# Revit family: Gira_053500
name_source: partatom
category: Electrical Fixtures
revit_build: Autodesk Revit 2017 (Build: 20160225_1515(x64)
units: mm (PartAtom-declared; Revit-internal decimal feet)

## family parameters
Cut with Voids When Loaded = No
Host = Face
Maintain Annotation Orientation = No
Part Type = Normal
Room Calculation Point = No
Round Connector Dimension = Use Diameter
Shared = No

## types (1)
- DC pow.supply 24 V 5 A DRA Electronics
    BIM = https://media.live.bim.site 00_REG 6.rfa
    BIMSITE_PRODUCT_ID = 66304a2bba27a85c9a5d9a86d3c19f51ab19208a
    Cost = 0 $
    Default Elevation = 1219 mm
    Description = DC PSU 24V 5A DRA Elec. Power supply DC 24 V 5 A,DRA Features: - Stabilised and short-circuit-proof switched mode power supply unit for installation on a top-hat rail.
    GTIN = 4010337535003
    HAN = 053500
    HeinzeBIM = https://www.heinze.de
    Manufacturer = Gira
    URL = https://www.gira.de

## geometry (parser evidence)
native form markers: Blend x2, Sweep x3
no freeform markers — native parametric forms only
